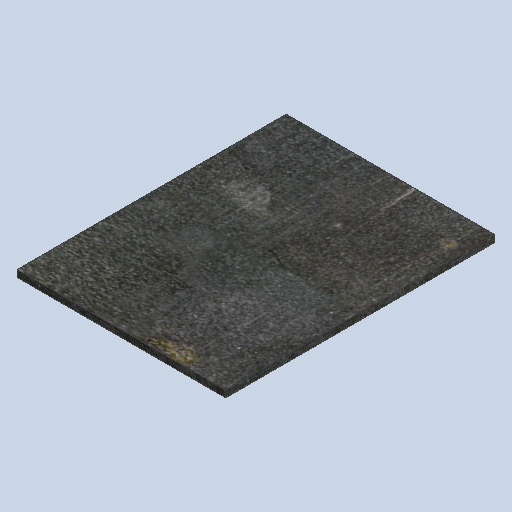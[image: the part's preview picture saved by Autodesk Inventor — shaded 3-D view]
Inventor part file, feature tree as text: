
AUTODESK INVENTOR PART (.ipt)
format: ipt  version: 2024.3 (Build 283343000, 343)  size: 228,864 bytes
history: native  units: mm
features: extrude x1, sketch x1
ambient origin geometry x8: Origin, YZ Plane, XZ Plane, XY Plane, X Axis, Y Axis, Z Axis, Center Point
bodies: Solid1 (feature_tree)
feature tree (2):
  extrude  "Extrusion1"  Depth=93.0mm
  sketch  "Sketch1"  dims[d0=120.0mm d1=93.0mm d2=3.0mm d3=0.0mm]
